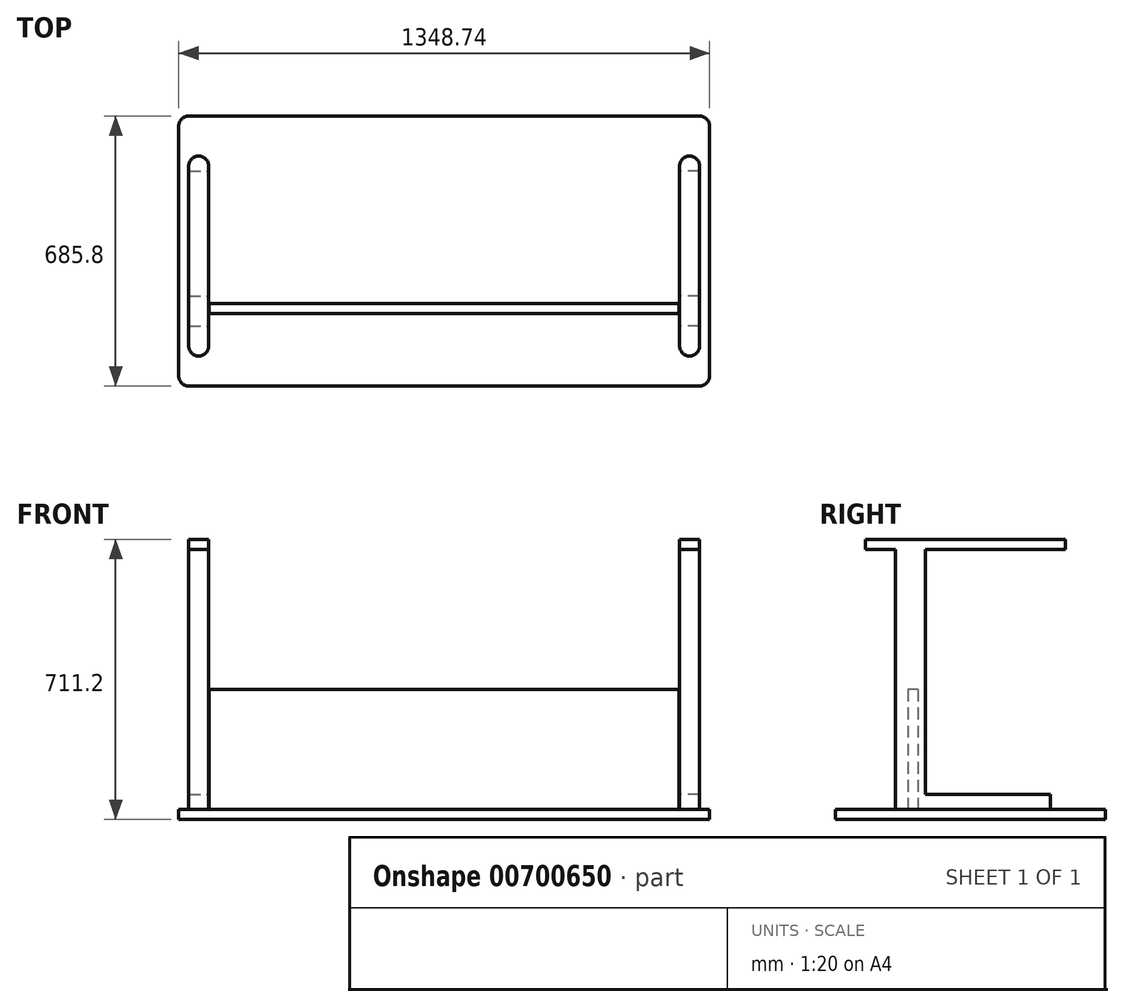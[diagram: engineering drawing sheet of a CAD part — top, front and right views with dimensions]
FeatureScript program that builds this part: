
annotation { "Feature Type Name" : "Feature", "Feature Type Description" : "" }
export const myFeature = defineFeature(function(context is Context, id is Id, definition is map)
    precondition{}
    {
        {
            var Q0;
            Q0=qCreatedBy(makeId("Top.planeOp"),FACE);
            var sketch = newSketch(context, id + "F0", { "sketchPlane" : qUnion([Q0])});
            skLineSegment(sketch, "E0.bottom", {"start": v(-674.37, 342.9) * mm, "end": v(674.37, 342.9) * mm});
            skLineSegment(sketch, "E0.top", {"start": v(-674.37, -342.9) * mm, "end": v(674.37, -342.9) * mm});
            skLineSegment(sketch, "E0.left", {"start": v(-674.37, 342.9) * mm, "end": v(-674.37, -342.9) * mm});
            skLineSegment(sketch, "E0.right", {"start": v(674.37, 342.9) * mm, "end": v(674.37, -342.9) * mm});
            skPoint(sketch, "E0.middle", {"position": v(0, 0) * mm});
            skSolve(sketch);
        }
        {
            var Q0;
            Q0=makeQuery(id+"F0.imprint","IMPRINT",FACE,{"disambiguationData":[TD([[makeQuery(id+"F0.imprint","IMPRINT",EDGE,{"derivedFrom":sQuery(id+"F0.wireOp",EDGE,"E0.bottom")}),-1.0]])]});
            extrude(context, id + "F1", {"entities" : qUnion([Q0]), "depth" : 25.4 * mm, "offsetDistance" : 25.4 * mm});
        }
        {
            var Q0;
            Q0=makeQuery(id+"F1.opExtrude","CAP_FACE",FACE,{"disambiguationData":[OSD([sQuery(id+"F0.wireOp",EDGE,"E0.bottom"),sQuery(id+"F0.wireOp",EDGE,"E0.top"),sQuery(id+"F0.wireOp",EDGE,"E0.left"),sQuery(id+"F0.wireOp",EDGE,"E0.right")])],"isStart":false});
            var sketch = newSketch(context, id + "F2", { "sketchPlane" : qUnion([Q0])});
            skLineSegment(sketch, "E1", {"start": v(0, 0) * mm, "end": v(0, 342.9) * mm});
            skLineSegment(sketch, "E2", {"start": v(0, 0) * mm, "end": v(0, -342.9) * mm});
            skSolve(sketch);
        }
        {
            var Q0;
            {var subQ2=sQuery(id+"F2.wireOp",EDGE,"E1");Q0=makeQuery(id+"F2.imprint","IMPRINT",FACE,{"disambiguationData":[TD([[makeQuery(id+"F2.imprint","IMPRINT",EDGE,{"derivedFrom":subQ2}),1.0]])]});}
            var sketch = newSketch(context, id + "F3", { "sketchPlane" : qUnion([Q0])});
            skLineSegment(sketch, "E3.bottom", {"start": v(-648.97, 203.2) * mm, "end": v(-598.17, 203.2) * mm});
            skLineSegment(sketch, "E3.top", {"start": v(-648.97, -114.3) * mm, "end": v(-598.17, -114.3) * mm});
            skLineSegment(sketch, "E3.left", {"start": v(-648.97, 203.2) * mm, "end": v(-648.97, -114.3) * mm});
            skLineSegment(sketch, "E3.right", {"start": v(-598.17, 203.2) * mm, "end": v(-598.17, -114.3) * mm});
            skLineSegment(sketch, "E4.MirrorCS", {"start": v(598.17, 203.2) * mm, "end": v(598.17, -114.3) * mm});
            skLineSegment(sketch, "E5.MirrorCS", {"start": v(648.97, 203.2) * mm, "end": v(598.17, 203.2) * mm});
            skLineSegment(sketch, "E6.MirrorCS", {"start": v(648.97, 203.2) * mm, "end": v(648.97, -114.3) * mm});
            skLineSegment(sketch, "E7.MirrorCS", {"start": v(648.97, -114.3) * mm, "end": v(598.17, -114.3) * mm});
            skSolve(sketch);
        }
        {
            var Q0;
            Q0 = qSketchRegion(id + "F3", true);
            extrude(context, id + "F4", {"entities" : qUnion([Q0]), "operationType" : NewBodyOperationType.ADD, "depth" : 38.1 * mm, "offsetDistance" : 25.4 * mm});
        }
        {
            var Q0;
            {var subQ2=sQuery(id+"F2.wireOp",EDGE,"E1");Q0=makeQuery(id+"F2.imprint","IMPRINT",FACE,{"disambiguationData":[TD([[makeQuery(id+"F2.imprint","IMPRINT",EDGE,{"derivedFrom":subQ2}),1.0]])]});}
            var sketch = newSketch(context, id + "F5", { "sketchPlane" : qUnion([Q0])});
            skLineSegment(sketch, "E8.bottom", {"start": v(-648.97, -114.3) * mm, "end": v(-598.17, -114.3) * mm});
            skLineSegment(sketch, "E8.top", {"start": v(-648.97, -190.5) * mm, "end": v(-598.17, -190.5) * mm});
            skLineSegment(sketch, "E8.left", {"start": v(-648.97, -114.3) * mm, "end": v(-648.97, -190.5) * mm});
            skLineSegment(sketch, "E8.right", {"start": v(-598.17, -114.3) * mm, "end": v(-598.17, -190.5) * mm});
            skLineSegment(sketch, "E9.MirrorCS", {"start": v(648.97, -190.5) * mm, "end": v(598.17, -190.5) * mm});
            skLineSegment(sketch, "E10.MirrorCS", {"start": v(648.97, -114.3) * mm, "end": v(648.97, -190.5) * mm});
            skLineSegment(sketch, "E11.MirrorCS", {"start": v(598.17, -114.3) * mm, "end": v(598.17, -190.5) * mm});
            skLineSegment(sketch, "E12.MirrorCS", {"start": v(648.97, -114.3) * mm, "end": v(598.17, -114.3) * mm});
            skSolve(sketch);
        }
        {
            var Q0;
            Q0 = qSketchRegion(id + "F5", true);
            extrude(context, id + "F6", {"entities" : qUnion([Q0]), "operationType" : NewBodyOperationType.ADD, "depth" : 660.4 * mm, "offsetDistance" : 25.4 * mm});
        }
        {
            var Q0;
            Q0=makeQuery(id+"F6.opExtrude","CAP_FACE",FACE,{"disambiguationData":[OSD([sQuery(id+"F5.wireOp",EDGE,"E8.bottom"),sQuery(id+"F5.wireOp",EDGE,"E8.top"),sQuery(id+"F5.wireOp",EDGE,"E8.left"),sQuery(id+"F5.wireOp",EDGE,"E8.right")])],"isStart":false});
            var sketch = newSketch(context, id + "F7", { "sketchPlane" : qUnion([Q0])});
            skLineSegment(sketch, "E13.bottom", {"start": v(-623.57, 241.3) * mm, "end": v(-623.57, 241.3) * mm});
            skLineSegment(sketch, "E13.top", {"start": v(-623.57, -266.7) * mm, "end": v(-623.57, -266.7) * mm});
            skLineSegment(sketch, "E13.left", {"start": v(-648.97, 215.9) * mm, "end": v(-648.97, -241.3) * mm});
            skLineSegment(sketch, "E13.right", {"start": v(-598.17, 215.9) * mm, "end": v(-598.17, -241.3) * mm});
            skPoint(sketch, "E14.visualSharp", {"position": v(-648.97, 241.3) * mm});
            skArc(sketch, "E14.filletArc", {"start": v(-623.57, 241.3) * mm, "mid": v(-641.53, 233.86) * mm, "end": v(-648.97, 215.9) * mm});
            skPoint(sketch, "E15.visualSharp", {"position": v(-598.17, 241.3) * mm});
            skArc(sketch, "E15.filletArc", {"start": v(-598.17, 215.9) * mm, "mid": v(-605.6, 233.86) * mm, "end": v(-623.57, 241.3) * mm});
            skPoint(sketch, "E16.visualSharp", {"position": v(-648.97, -266.7) * mm});
            skArc(sketch, "E16.filletArc", {"start": v(-648.97, -241.3) * mm, "mid": v(-641.53, -259.26) * mm, "end": v(-623.57, -266.7) * mm});
            skPoint(sketch, "E17.visualSharp", {"position": v(-598.17, -266.7) * mm});
            skArc(sketch, "E17.filletArc", {"start": v(-623.57, -266.7) * mm, "mid": v(-605.6, -259.26) * mm, "end": v(-598.17, -241.3) * mm});
            skLineSegment(sketch, "E18.MirrorCS", {"start": v(648.97, 215.9) * mm, "end": v(648.97, -241.3) * mm});
            skLineSegment(sketch, "E19.MirrorCS", {"start": v(598.17, 215.9) * mm, "end": v(598.17, -241.3) * mm});
            skArc(sketch, "E20.MirrorCS", {"start": v(648.97, -241.3) * mm, "mid": v(641.53, -259.26) * mm, "end": v(623.57, -266.7) * mm});
            skArc(sketch, "E21.MirrorCS", {"start": v(623.57, -266.7) * mm, "mid": v(605.6, -259.26) * mm, "end": v(598.17, -241.3) * mm});
            skArc(sketch, "E22.MirrorCS", {"start": v(598.17, 215.9) * mm, "mid": v(605.6, 233.86) * mm, "end": v(623.57, 241.3) * mm});
            skArc(sketch, "E23.MirrorCS", {"start": v(623.57, 241.3) * mm, "mid": v(641.53, 233.86) * mm, "end": v(648.97, 215.9) * mm});
            skSolve(sketch);
        }
        {
            var Q0;
            Q0 = qSketchRegion(id + "F7", true);
            extrude(context, id + "F8", {"entities" : qUnion([Q0]), "operationType" : NewBodyOperationType.ADD, "depth" : 25.4 * mm, "offsetDistance" : 25.4 * mm});
        }
        {
            var Q0;
            {var subQ2=sQuery(id+"F2.wireOp",EDGE,"E1");Q0=makeQuery(id+"F2.imprint","IMPRINT",FACE,{"disambiguationData":[TD([[makeQuery(id+"F2.imprint","IMPRINT",EDGE,{"derivedFrom":subQ2}),1.0]])]});}
            var sketch = newSketch(context, id + "F9", { "sketchPlane" : qUnion([Q0])});
            skLineSegment(sketch, "E24.bottom", {"start": v(-597.54, -133.17) * mm, "end": v(597.13, -133.17) * mm});
            skLineSegment(sketch, "E24.top", {"start": v(-597.54, -158.76) * mm, "end": v(597.13, -158.76) * mm});
            skLineSegment(sketch, "E24.left", {"start": v(-597.54, -133.17) * mm, "end": v(-597.54, -158.76) * mm});
            skLineSegment(sketch, "E24.right", {"start": v(597.13, -133.17) * mm, "end": v(597.13, -158.76) * mm});
            skSolve(sketch);
        }
        {
            var Q0;
            Q0 = qSketchRegion(id + "F9", true);
            extrude(context, id + "F10", {"entities" : qUnion([Q0]), "operationType" : NewBodyOperationType.ADD, "depth" : 304.8 * mm, "offsetDistance" : 25.4 * mm});
        }
        {
            var Q0;
            Q0=makeQuery(id+"F1.opExtrude","SWEPT_EDGE",EDGE,{"disambiguationData":[OSD([sQuery(id+"F0.wireOp",EDGE,"E0.bottom"),sQuery(id+"F0.wireOp",EDGE,"E0.left")])]});
            fillet(context, id + "F11", {"entities" : qUnion([Q0]), "radius" : 25.4 * mm, "tangentPropagation" : true, "allowEdgeOverflow" : false});
        }
        {
            var Q0;
            Q0=makeQuery(id+"F1.opExtrude","SWEPT_EDGE",EDGE,{"disambiguationData":[OSD([sQuery(id+"F0.wireOp",EDGE,"E0.top"),sQuery(id+"F0.wireOp",EDGE,"E0.left")])]});
            fillet(context, id + "F12", {"entities" : qUnion([Q0]), "radius" : 25.4 * mm, "tangentPropagation" : true, "allowEdgeOverflow" : false});
        }
        {
            var Q0;
            Q0=makeQuery(id+"F1.opExtrude","SWEPT_EDGE",EDGE,{"disambiguationData":[OSD([sQuery(id+"F0.wireOp",EDGE,"E0.top"),sQuery(id+"F0.wireOp",EDGE,"E0.right")])]});
            fillet(context, id + "F13", {"entities" : qUnion([Q0]), "radius" : 25.4 * mm, "tangentPropagation" : true, "allowEdgeOverflow" : false});
        }
        {
            var Q0;
            Q0=makeQuery(id+"F1.opExtrude","SWEPT_EDGE",EDGE,{"disambiguationData":[OSD([sQuery(id+"F0.wireOp",EDGE,"E0.bottom"),sQuery(id+"F0.wireOp",EDGE,"E0.right")])]});
            fillet(context, id + "F14", {"entities" : qUnion([Q0]), "radius" : 25.4 * mm, "tangentPropagation" : true, "allowEdgeOverflow" : false});
        }
    });
